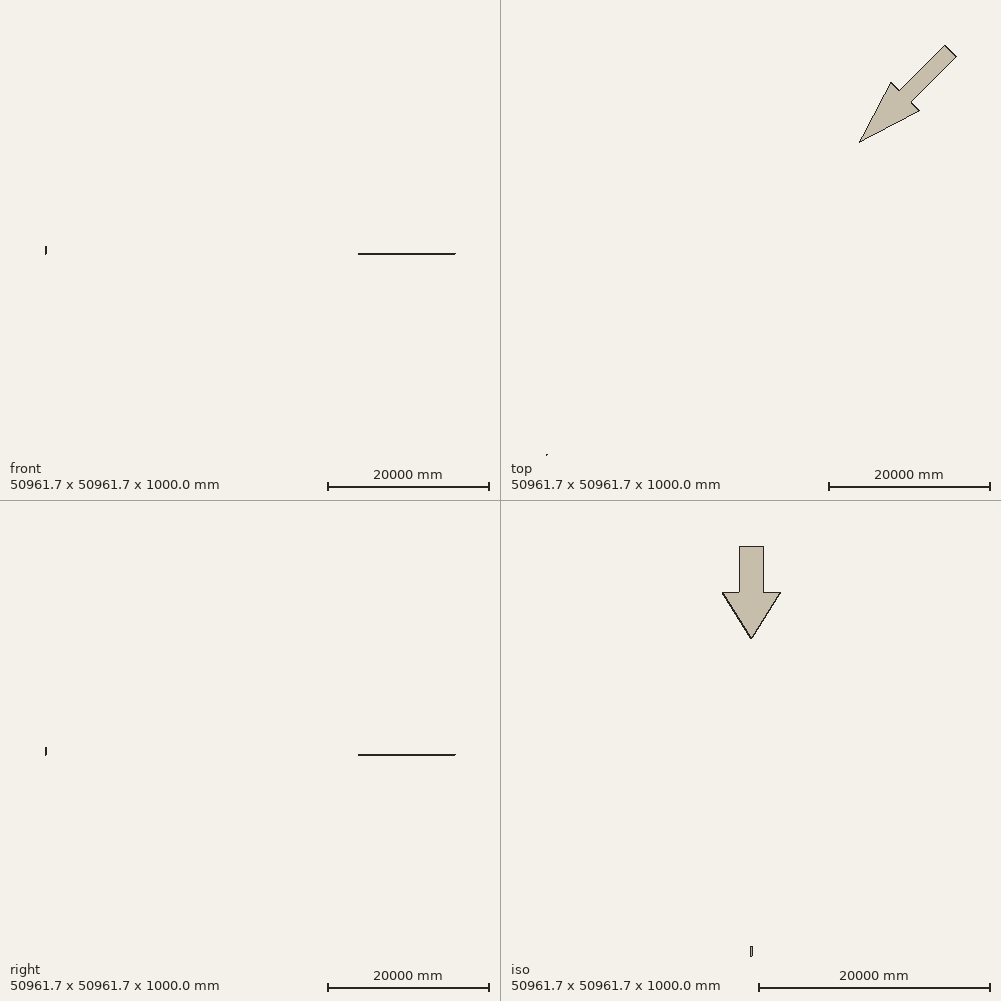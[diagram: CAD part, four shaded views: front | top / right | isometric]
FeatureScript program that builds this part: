
annotation { "Feature Type Name" : "Feature", "Feature Type Description" : "" }
export const myFeature = defineFeature(function(context is Context, id is Id, definition is map)
    precondition{}
    {
        {
            var Q0;
            Q0=qCreatedBy(makeId("Top.planeOp"),FACE);
            var sketch = newSketch(context, id + "F0", { "sketchPlane" : qUnion([Q0])});
            skLineSegment(sketch, "E0", {"start": v(0, -8.09) * mm, "end": v(0, 84.63) * mm, "construction": true});
            skLineSegment(sketch, "E1", {"start": v(-1000, 8000) * mm, "end": v(1000, 8000) * mm});
            skLineSegment(sketch, "E2", {"start": v(1000, 8000) * mm, "end": v(1000, 0) * mm});
            skLineSegment(sketch, "E3", {"start": v(1000, 0) * mm, "end": v(2500, 0) * mm});
            skLineSegment(sketch, "E4", {"start": v(2500, 0) * mm, "end": v(0, -8000) * mm});
            skLineSegment(sketch, "E5", {"start": v(0, -8000) * mm, "end": v(-2500, 0) * mm});
            skLineSegment(sketch, "E6", {"start": v(-2500, 0) * mm, "end": v(-1000, 0) * mm});
            skLineSegment(sketch, "E7", {"start": v(-1000, 0) * mm, "end": v(-1000, 8000) * mm});
            skSolve(sketch);
        }
        {
            var Q0;
            Q0 = qSketchRegion(id + "F0", true);
            extrude(context, id + "F1", {"entities" : qUnion([Q0]), "depth" : 100 * mm, "offsetDistance" : 25 * mm});
        }
        {
            var Q0;
            Q0=qCreatedBy(makeId("Top.planeOp"),FACE);
            var sketch = newSketch(context, id + "F2", { "sketchPlane" : qUnion([Q0])});
            skCircle(sketch, "E8", {"center": v(0, -63000) * mm, "radius": 50 * mm});
            skSolve(sketch);
        }
        {
            var Q0;
            Q0 = qSketchRegion(id + "F2", true);
            extrude(context, id + "F3", {"entities" : qUnion([Q0]), "depth" : 1000 * mm, "offsetDistance" : 25 * mm});
        }
        {
            var Q0;
            Q0=makeQuery(id+"F1.opExtrude","SWEPT_BODY",BODY,{"disambiguationData":[OSD([sQuery(id+"F0.wireOp",EDGE,"E1"),sQuery(id+"F0.wireOp",EDGE,"E2"),sQuery(id+"F0.wireOp",EDGE,"E3"),sQuery(id+"F0.wireOp",EDGE,"E4"),sQuery(id+"F0.wireOp",EDGE,"E5"),sQuery(id+"F0.wireOp",EDGE,"E6"),sQuery(id+"F0.wireOp",EDGE,"E7")])]});
            var Q1;
            Q1=makeQuery(id+"F1.opExtrude","SWEPT_BODY",BODY,{"disambiguationData":[OSD([sQuery(id+"F0.wireOp",EDGE,"40971db5-e6c9-45f8-a843-42a628b66c5b.sketch_text.stroke-86"),sQuery(id+"F0.wireOp",EDGE,"40971db5-e6c9-45f8-a843-42a628b66c5b.sketch_text.stroke-87"),sQuery(id+"F0.wireOp",EDGE,"40971db5-e6c9-45f8-a843-42a628b66c5b.sketch_text.stroke-88"),sQuery(id+"F0.wireOp",EDGE,"40971db5-e6c9-45f8-a843-42a628b66c5b.sketch_text.stroke-89")])]});
            var Q2;
            Q2=makeQuery(id+"F1.opExtrude","SWEPT_BODY",BODY,{"disambiguationData":[OSD([sQuery(id+"F0.wireOp",EDGE,"40971db5-e6c9-45f8-a843-42a628b66c5b.sketch_text.stroke-90"),sQuery(id+"F0.wireOp",EDGE,"40971db5-e6c9-45f8-a843-42a628b66c5b.sketch_text.stroke-91"),sQuery(id+"F0.wireOp",EDGE,"40971db5-e6c9-45f8-a843-42a628b66c5b.sketch_text.stroke-92"),sQuery(id+"F0.wireOp",EDGE,"40971db5-e6c9-45f8-a843-42a628b66c5b.sketch_text.stroke-93"),sQuery(id+"F0.wireOp",EDGE,"40971db5-e6c9-45f8-a843-42a628b66c5b.sketch_text.stroke-94"),sQuery(id+"F0.wireOp",EDGE,"40971db5-e6c9-45f8-a843-42a628b66c5b.sketch_text.stroke-95"),sQuery(id+"F0.wireOp",EDGE,"40971db5-e6c9-45f8-a843-42a628b66c5b.sketch_text.stroke-96"),sQuery(id+"F0.wireOp",EDGE,"40971db5-e6c9-45f8-a843-42a628b66c5b.sketch_text.stroke-97")])]});
            var Q3;
            Q3=makeQuery(id+"F1.opExtrude","SWEPT_BODY",BODY,{"disambiguationData":[OSD([sQuery(id+"F0.wireOp",EDGE,"40971db5-e6c9-45f8-a843-42a628b66c5b.sketch_text.stroke-32"),sQuery(id+"F0.wireOp",EDGE,"40971db5-e6c9-45f8-a843-42a628b66c5b.sketch_text.stroke-33"),sQuery(id+"F0.wireOp",EDGE,"40971db5-e6c9-45f8-a843-42a628b66c5b.sketch_text.stroke-34"),sQuery(id+"F0.wireOp",EDGE,"40971db5-e6c9-45f8-a843-42a628b66c5b.sketch_text.stroke-35"),sQuery(id+"F0.wireOp",EDGE,"40971db5-e6c9-45f8-a843-42a628b66c5b.sketch_text.stroke-36"),sQuery(id+"F0.wireOp",EDGE,"40971db5-e6c9-45f8-a843-42a628b66c5b.sketch_text.stroke-37"),sQuery(id+"F0.wireOp",EDGE,"40971db5-e6c9-45f8-a843-42a628b66c5b.sketch_text.stroke-38"),sQuery(id+"F0.wireOp",EDGE,"40971db5-e6c9-45f8-a843-42a628b66c5b.sketch_text.stroke-39"),sQuery(id+"F0.wireOp",EDGE,"40971db5-e6c9-45f8-a843-42a628b66c5b.sketch_text.stroke-40"),sQuery(id+"F0.wireOp",EDGE,"40971db5-e6c9-45f8-a843-42a628b66c5b.sketch_text.stroke-41"),sQuery(id+"F0.wireOp",EDGE,"40971db5-e6c9-45f8-a843-42a628b66c5b.sketch_text.stroke-42"),sQuery(id+"F0.wireOp",EDGE,"40971db5-e6c9-45f8-a843-42a628b66c5b.sketch_text.stroke-43"),sQuery(id+"F0.wireOp",EDGE,"40971db5-e6c9-45f8-a843-42a628b66c5b.sketch_text.stroke-44"),sQuery(id+"F0.wireOp",EDGE,"40971db5-e6c9-45f8-a843-42a628b66c5b.sketch_text.stroke-45"),sQuery(id+"F0.wireOp",EDGE,"40971db5-e6c9-45f8-a843-42a628b66c5b.sketch_text.stroke-46"),sQuery(id+"F0.wireOp",EDGE,"40971db5-e6c9-45f8-a843-42a628b66c5b.sketch_text.stroke-47"),sQuery(id+"F0.wireOp",EDGE,"40971db5-e6c9-45f8-a843-42a628b66c5b.sketch_text.stroke-48")])]});
            var Q4;
            Q4=makeQuery(id+"F1.opExtrude","SWEPT_BODY",BODY,{"disambiguationData":[OSD([sQuery(id+"F0.wireOp",EDGE,"40971db5-e6c9-45f8-a843-42a628b66c5b.sketch_text.stroke-73"),sQuery(id+"F0.wireOp",EDGE,"40971db5-e6c9-45f8-a843-42a628b66c5b.sketch_text.stroke-74"),sQuery(id+"F0.wireOp",EDGE,"40971db5-e6c9-45f8-a843-42a628b66c5b.sketch_text.stroke-75"),sQuery(id+"F0.wireOp",EDGE,"40971db5-e6c9-45f8-a843-42a628b66c5b.sketch_text.stroke-76"),sQuery(id+"F0.wireOp",EDGE,"40971db5-e6c9-45f8-a843-42a628b66c5b.sketch_text.stroke-77"),sQuery(id+"F0.wireOp",EDGE,"40971db5-e6c9-45f8-a843-42a628b66c5b.sketch_text.stroke-78"),sQuery(id+"F0.wireOp",EDGE,"40971db5-e6c9-45f8-a843-42a628b66c5b.sketch_text.stroke-79"),sQuery(id+"F0.wireOp",EDGE,"40971db5-e6c9-45f8-a843-42a628b66c5b.sketch_text.stroke-80"),sQuery(id+"F0.wireOp",EDGE,"40971db5-e6c9-45f8-a843-42a628b66c5b.sketch_text.stroke-81"),sQuery(id+"F0.wireOp",EDGE,"40971db5-e6c9-45f8-a843-42a628b66c5b.sketch_text.stroke-82"),sQuery(id+"F0.wireOp",EDGE,"40971db5-e6c9-45f8-a843-42a628b66c5b.sketch_text.stroke-83"),sQuery(id+"F0.wireOp",EDGE,"40971db5-e6c9-45f8-a843-42a628b66c5b.sketch_text.stroke-84"),sQuery(id+"F0.wireOp",EDGE,"40971db5-e6c9-45f8-a843-42a628b66c5b.sketch_text.stroke-85")])]});
            var Q5;
            Q5=makeQuery(id+"F1.opExtrude","SWEPT_BODY",BODY,{"disambiguationData":[OSD([sQuery(id+"F0.wireOp",EDGE,"40971db5-e6c9-45f8-a843-42a628b66c5b.sketch_text.stroke-113"),sQuery(id+"F0.wireOp",EDGE,"40971db5-e6c9-45f8-a843-42a628b66c5b.sketch_text.stroke-114"),sQuery(id+"F0.wireOp",EDGE,"40971db5-e6c9-45f8-a843-42a628b66c5b.sketch_text.stroke-115"),sQuery(id+"F0.wireOp",EDGE,"40971db5-e6c9-45f8-a843-42a628b66c5b.sketch_text.stroke-116"),sQuery(id+"F0.wireOp",EDGE,"40971db5-e6c9-45f8-a843-42a628b66c5b.sketch_text.stroke-117"),sQuery(id+"F0.wireOp",EDGE,"40971db5-e6c9-45f8-a843-42a628b66c5b.sketch_text.stroke-118"),sQuery(id+"F0.wireOp",EDGE,"40971db5-e6c9-45f8-a843-42a628b66c5b.sketch_text.stroke-119"),sQuery(id+"F0.wireOp",EDGE,"40971db5-e6c9-45f8-a843-42a628b66c5b.sketch_text.stroke-120"),sQuery(id+"F0.wireOp",EDGE,"40971db5-e6c9-45f8-a843-42a628b66c5b.sketch_text.stroke-121"),sQuery(id+"F0.wireOp",EDGE,"40971db5-e6c9-45f8-a843-42a628b66c5b.sketch_text.stroke-122"),sQuery(id+"F0.wireOp",EDGE,"40971db5-e6c9-45f8-a843-42a628b66c5b.sketch_text.stroke-123"),sQuery(id+"F0.wireOp",EDGE,"40971db5-e6c9-45f8-a843-42a628b66c5b.sketch_text.stroke-124"),sQuery(id+"F0.wireOp",EDGE,"40971db5-e6c9-45f8-a843-42a628b66c5b.sketch_text.stroke-125"),sQuery(id+"F0.wireOp",EDGE,"40971db5-e6c9-45f8-a843-42a628b66c5b.sketch_text.stroke-126"),sQuery(id+"F0.wireOp",EDGE,"40971db5-e6c9-45f8-a843-42a628b66c5b.sketch_text.stroke-127"),sQuery(id+"F0.wireOp",EDGE,"40971db5-e6c9-45f8-a843-42a628b66c5b.sketch_text.stroke-128"),sQuery(id+"F0.wireOp",EDGE,"40971db5-e6c9-45f8-a843-42a628b66c5b.sketch_text.stroke-129"),sQuery(id+"F0.wireOp",EDGE,"40971db5-e6c9-45f8-a843-42a628b66c5b.sketch_text.stroke-130")])]});
            var Q6;
            Q6=makeQuery(id+"F1.opExtrude","SWEPT_BODY",BODY,{"disambiguationData":[OSD([sQuery(id+"F0.wireOp",EDGE,"40971db5-e6c9-45f8-a843-42a628b66c5b.sketch_text.stroke-20"),sQuery(id+"F0.wireOp",EDGE,"40971db5-e6c9-45f8-a843-42a628b66c5b.sketch_text.stroke-21"),sQuery(id+"F0.wireOp",EDGE,"40971db5-e6c9-45f8-a843-42a628b66c5b.sketch_text.stroke-22"),sQuery(id+"F0.wireOp",EDGE,"40971db5-e6c9-45f8-a843-42a628b66c5b.sketch_text.stroke-23")])]});
            var Q7;
            Q7=makeQuery(id+"F1.opExtrude","SWEPT_BODY",BODY,{"disambiguationData":[OSD([sQuery(id+"F0.wireOp",EDGE,"40971db5-e6c9-45f8-a843-42a628b66c5b.sketch_text.stroke-98"),sQuery(id+"F0.wireOp",EDGE,"40971db5-e6c9-45f8-a843-42a628b66c5b.sketch_text.stroke-99"),sQuery(id+"F0.wireOp",EDGE,"40971db5-e6c9-45f8-a843-42a628b66c5b.sketch_text.stroke-100"),sQuery(id+"F0.wireOp",EDGE,"40971db5-e6c9-45f8-a843-42a628b66c5b.sketch_text.stroke-101"),sQuery(id+"F0.wireOp",EDGE,"40971db5-e6c9-45f8-a843-42a628b66c5b.sketch_text.stroke-102"),sQuery(id+"F0.wireOp",EDGE,"40971db5-e6c9-45f8-a843-42a628b66c5b.sketch_text.stroke-103"),sQuery(id+"F0.wireOp",EDGE,"40971db5-e6c9-45f8-a843-42a628b66c5b.sketch_text.stroke-104"),sQuery(id+"F0.wireOp",EDGE,"40971db5-e6c9-45f8-a843-42a628b66c5b.sketch_text.stroke-105"),sQuery(id+"F0.wireOp",EDGE,"40971db5-e6c9-45f8-a843-42a628b66c5b.sketch_text.stroke-106"),sQuery(id+"F0.wireOp",EDGE,"40971db5-e6c9-45f8-a843-42a628b66c5b.sketch_text.stroke-107"),sQuery(id+"F0.wireOp",EDGE,"40971db5-e6c9-45f8-a843-42a628b66c5b.sketch_text.stroke-108"),sQuery(id+"F0.wireOp",EDGE,"40971db5-e6c9-45f8-a843-42a628b66c5b.sketch_text.stroke-109"),sQuery(id+"F0.wireOp",EDGE,"40971db5-e6c9-45f8-a843-42a628b66c5b.sketch_text.stroke-110"),sQuery(id+"F0.wireOp",EDGE,"40971db5-e6c9-45f8-a843-42a628b66c5b.sketch_text.stroke-111"),sQuery(id+"F0.wireOp",EDGE,"40971db5-e6c9-45f8-a843-42a628b66c5b.sketch_text.stroke-112")])]});
            var Q8;
            Q8=makeQuery(id+"F1.opExtrude","SWEPT_BODY",BODY,{"disambiguationData":[OSD([sQuery(id+"F0.wireOp",EDGE,"40971db5-e6c9-45f8-a843-42a628b66c5b.sketch_text.stroke-184"),sQuery(id+"F0.wireOp",EDGE,"40971db5-e6c9-45f8-a843-42a628b66c5b.sketch_text.stroke-185"),sQuery(id+"F0.wireOp",EDGE,"40971db5-e6c9-45f8-a843-42a628b66c5b.sketch_text.stroke-186"),sQuery(id+"F0.wireOp",EDGE,"40971db5-e6c9-45f8-a843-42a628b66c5b.sketch_text.stroke-187"),sQuery(id+"F0.wireOp",EDGE,"40971db5-e6c9-45f8-a843-42a628b66c5b.sketch_text.stroke-188"),sQuery(id+"F0.wireOp",EDGE,"40971db5-e6c9-45f8-a843-42a628b66c5b.sketch_text.stroke-189"),sQuery(id+"F0.wireOp",EDGE,"40971db5-e6c9-45f8-a843-42a628b66c5b.sketch_text.stroke-190"),sQuery(id+"F0.wireOp",EDGE,"40971db5-e6c9-45f8-a843-42a628b66c5b.sketch_text.stroke-191"),sQuery(id+"F0.wireOp",EDGE,"40971db5-e6c9-45f8-a843-42a628b66c5b.sketch_text.stroke-192"),sQuery(id+"F0.wireOp",EDGE,"40971db5-e6c9-45f8-a843-42a628b66c5b.sketch_text.stroke-193"),sQuery(id+"F0.wireOp",EDGE,"40971db5-e6c9-45f8-a843-42a628b66c5b.sketch_text.stroke-194"),sQuery(id+"F0.wireOp",EDGE,"40971db5-e6c9-45f8-a843-42a628b66c5b.sketch_text.stroke-195"),sQuery(id+"F0.wireOp",EDGE,"40971db5-e6c9-45f8-a843-42a628b66c5b.sketch_text.stroke-196"),sQuery(id+"F0.wireOp",EDGE,"40971db5-e6c9-45f8-a843-42a628b66c5b.sketch_text.stroke-197"),sQuery(id+"F0.wireOp",EDGE,"40971db5-e6c9-45f8-a843-42a628b66c5b.sketch_text.stroke-198"),sQuery(id+"F0.wireOp",EDGE,"40971db5-e6c9-45f8-a843-42a628b66c5b.sketch_text.stroke-199"),sQuery(id+"F0.wireOp",EDGE,"40971db5-e6c9-45f8-a843-42a628b66c5b.sketch_text.stroke-200"),sQuery(id+"F0.wireOp",EDGE,"40971db5-e6c9-45f8-a843-42a628b66c5b.sketch_text.stroke-201"),sQuery(id+"F0.wireOp",EDGE,"40971db5-e6c9-45f8-a843-42a628b66c5b.sketch_text.stroke-202"),sQuery(id+"F0.wireOp",EDGE,"40971db5-e6c9-45f8-a843-42a628b66c5b.sketch_text.stroke-203"),sQuery(id+"F0.wireOp",EDGE,"40971db5-e6c9-45f8-a843-42a628b66c5b.sketch_text.stroke-204"),sQuery(id+"F0.wireOp",EDGE,"40971db5-e6c9-45f8-a843-42a628b66c5b.sketch_text.stroke-205"),sQuery(id+"F0.wireOp",EDGE,"40971db5-e6c9-45f8-a843-42a628b66c5b.sketch_text.stroke-206"),sQuery(id+"F0.wireOp",EDGE,"40971db5-e6c9-45f8-a843-42a628b66c5b.sketch_text.stroke-207"),sQuery(id+"F0.wireOp",EDGE,"40971db5-e6c9-45f8-a843-42a628b66c5b.sketch_text.stroke-208"),sQuery(id+"F0.wireOp",EDGE,"40971db5-e6c9-45f8-a843-42a628b66c5b.sketch_text.stroke-209"),sQuery(id+"F0.wireOp",EDGE,"40971db5-e6c9-45f8-a843-42a628b66c5b.sketch_text.stroke-210"),sQuery(id+"F0.wireOp",EDGE,"40971db5-e6c9-45f8-a843-42a628b66c5b.sketch_text.stroke-211"),sQuery(id+"F0.wireOp",EDGE,"40971db5-e6c9-45f8-a843-42a628b66c5b.sketch_text.stroke-212"),sQuery(id+"F0.wireOp",EDGE,"40971db5-e6c9-45f8-a843-42a628b66c5b.sketch_text.stroke-213"),sQuery(id+"F0.wireOp",EDGE,"40971db5-e6c9-45f8-a843-42a628b66c5b.sketch_text.stroke-214"),sQuery(id+"F0.wireOp",EDGE,"40971db5-e6c9-45f8-a843-42a628b66c5b.sketch_text.stroke-215"),sQuery(id+"F0.wireOp",EDGE,"40971db5-e6c9-45f8-a843-42a628b66c5b.sketch_text.stroke-216"),sQuery(id+"F0.wireOp",EDGE,"40971db5-e6c9-45f8-a843-42a628b66c5b.sketch_text.stroke-217"),sQuery(id+"F0.wireOp",EDGE,"40971db5-e6c9-45f8-a843-42a628b66c5b.sketch_text.stroke-218"),sQuery(id+"F0.wireOp",EDGE,"40971db5-e6c9-45f8-a843-42a628b66c5b.sketch_text.stroke-219"),sQuery(id+"F0.wireOp",EDGE,"40971db5-e6c9-45f8-a843-42a628b66c5b.sketch_text.stroke-220"),sQuery(id+"F0.wireOp",EDGE,"40971db5-e6c9-45f8-a843-42a628b66c5b.sketch_text.stroke-221"),sQuery(id+"F0.wireOp",EDGE,"40971db5-e6c9-45f8-a843-42a628b66c5b.sketch_text.stroke-222"),sQuery(id+"F0.wireOp",EDGE,"40971db5-e6c9-45f8-a843-42a628b66c5b.sketch_text.stroke-223"),sQuery(id+"F0.wireOp",EDGE,"40971db5-e6c9-45f8-a843-42a628b66c5b.sketch_text.stroke-224"),sQuery(id+"F0.wireOp",EDGE,"40971db5-e6c9-45f8-a843-42a628b66c5b.sketch_text.stroke-225"),sQuery(id+"F0.wireOp",EDGE,"40971db5-e6c9-45f8-a843-42a628b66c5b.sketch_text.stroke-226"),sQuery(id+"F0.wireOp",EDGE,"40971db5-e6c9-45f8-a843-42a628b66c5b.sketch_text.stroke-227")])]});
            var Q9;
            Q9=makeQuery(id+"F1.opExtrude","SWEPT_BODY",BODY,{"disambiguationData":[OSD([sQuery(id+"F0.wireOp",EDGE,"40971db5-e6c9-45f8-a843-42a628b66c5b.sketch_text.stroke-167"),sQuery(id+"F0.wireOp",EDGE,"40971db5-e6c9-45f8-a843-42a628b66c5b.sketch_text.stroke-168"),sQuery(id+"F0.wireOp",EDGE,"40971db5-e6c9-45f8-a843-42a628b66c5b.sketch_text.stroke-169"),sQuery(id+"F0.wireOp",EDGE,"40971db5-e6c9-45f8-a843-42a628b66c5b.sketch_text.stroke-170"),sQuery(id+"F0.wireOp",EDGE,"40971db5-e6c9-45f8-a843-42a628b66c5b.sketch_text.stroke-171"),sQuery(id+"F0.wireOp",EDGE,"40971db5-e6c9-45f8-a843-42a628b66c5b.sketch_text.stroke-172"),sQuery(id+"F0.wireOp",EDGE,"40971db5-e6c9-45f8-a843-42a628b66c5b.sketch_text.stroke-173"),sQuery(id+"F0.wireOp",EDGE,"40971db5-e6c9-45f8-a843-42a628b66c5b.sketch_text.stroke-174"),sQuery(id+"F0.wireOp",EDGE,"40971db5-e6c9-45f8-a843-42a628b66c5b.sketch_text.stroke-175"),sQuery(id+"F0.wireOp",EDGE,"40971db5-e6c9-45f8-a843-42a628b66c5b.sketch_text.stroke-176"),sQuery(id+"F0.wireOp",EDGE,"40971db5-e6c9-45f8-a843-42a628b66c5b.sketch_text.stroke-177"),sQuery(id+"F0.wireOp",EDGE,"40971db5-e6c9-45f8-a843-42a628b66c5b.sketch_text.stroke-178"),sQuery(id+"F0.wireOp",EDGE,"40971db5-e6c9-45f8-a843-42a628b66c5b.sketch_text.stroke-179"),sQuery(id+"F0.wireOp",EDGE,"40971db5-e6c9-45f8-a843-42a628b66c5b.sketch_text.stroke-180"),sQuery(id+"F0.wireOp",EDGE,"40971db5-e6c9-45f8-a843-42a628b66c5b.sketch_text.stroke-181"),sQuery(id+"F0.wireOp",EDGE,"40971db5-e6c9-45f8-a843-42a628b66c5b.sketch_text.stroke-182"),sQuery(id+"F0.wireOp",EDGE,"40971db5-e6c9-45f8-a843-42a628b66c5b.sketch_text.stroke-183")])]});
            var Q10;
            Q10=makeQuery(id+"F1.opExtrude","SWEPT_BODY",BODY,{"disambiguationData":[OSD([sQuery(id+"F0.wireOp",EDGE,"40971db5-e6c9-45f8-a843-42a628b66c5b.sketch_text.stroke-150"),sQuery(id+"F0.wireOp",EDGE,"40971db5-e6c9-45f8-a843-42a628b66c5b.sketch_text.stroke-151"),sQuery(id+"F0.wireOp",EDGE,"40971db5-e6c9-45f8-a843-42a628b66c5b.sketch_text.stroke-152"),sQuery(id+"F0.wireOp",EDGE,"40971db5-e6c9-45f8-a843-42a628b66c5b.sketch_text.stroke-153"),sQuery(id+"F0.wireOp",EDGE,"40971db5-e6c9-45f8-a843-42a628b66c5b.sketch_text.stroke-154"),sQuery(id+"F0.wireOp",EDGE,"40971db5-e6c9-45f8-a843-42a628b66c5b.sketch_text.stroke-155"),sQuery(id+"F0.wireOp",EDGE,"40971db5-e6c9-45f8-a843-42a628b66c5b.sketch_text.stroke-156"),sQuery(id+"F0.wireOp",EDGE,"40971db5-e6c9-45f8-a843-42a628b66c5b.sketch_text.stroke-157"),sQuery(id+"F0.wireOp",EDGE,"40971db5-e6c9-45f8-a843-42a628b66c5b.sketch_text.stroke-158"),sQuery(id+"F0.wireOp",EDGE,"40971db5-e6c9-45f8-a843-42a628b66c5b.sketch_text.stroke-159"),sQuery(id+"F0.wireOp",EDGE,"40971db5-e6c9-45f8-a843-42a628b66c5b.sketch_text.stroke-160"),sQuery(id+"F0.wireOp",EDGE,"40971db5-e6c9-45f8-a843-42a628b66c5b.sketch_text.stroke-161"),sQuery(id+"F0.wireOp",EDGE,"40971db5-e6c9-45f8-a843-42a628b66c5b.sketch_text.stroke-162"),sQuery(id+"F0.wireOp",EDGE,"40971db5-e6c9-45f8-a843-42a628b66c5b.sketch_text.stroke-163"),sQuery(id+"F0.wireOp",EDGE,"40971db5-e6c9-45f8-a843-42a628b66c5b.sketch_text.stroke-164"),sQuery(id+"F0.wireOp",EDGE,"40971db5-e6c9-45f8-a843-42a628b66c5b.sketch_text.stroke-165"),sQuery(id+"F0.wireOp",EDGE,"40971db5-e6c9-45f8-a843-42a628b66c5b.sketch_text.stroke-166")])]});
            var Q11;
            Q11=makeQuery(id+"F1.opExtrude","SWEPT_BODY",BODY,{"disambiguationData":[OSD([sQuery(id+"F0.wireOp",EDGE,"40971db5-e6c9-45f8-a843-42a628b66c5b.sketch_text.stroke-24"),sQuery(id+"F0.wireOp",EDGE,"40971db5-e6c9-45f8-a843-42a628b66c5b.sketch_text.stroke-25"),sQuery(id+"F0.wireOp",EDGE,"40971db5-e6c9-45f8-a843-42a628b66c5b.sketch_text.stroke-26"),sQuery(id+"F0.wireOp",EDGE,"40971db5-e6c9-45f8-a843-42a628b66c5b.sketch_text.stroke-27"),sQuery(id+"F0.wireOp",EDGE,"40971db5-e6c9-45f8-a843-42a628b66c5b.sketch_text.stroke-28"),sQuery(id+"F0.wireOp",EDGE,"40971db5-e6c9-45f8-a843-42a628b66c5b.sketch_text.stroke-29"),sQuery(id+"F0.wireOp",EDGE,"40971db5-e6c9-45f8-a843-42a628b66c5b.sketch_text.stroke-30"),sQuery(id+"F0.wireOp",EDGE,"40971db5-e6c9-45f8-a843-42a628b66c5b.sketch_text.stroke-31")])]});
            var Q12;
            Q12=makeQuery(id+"F1.opExtrude","SWEPT_BODY",BODY,{"disambiguationData":[OSD([sQuery(id+"F0.wireOp",EDGE,"40971db5-e6c9-45f8-a843-42a628b66c5b.sketch_text.stroke-0"),sQuery(id+"F0.wireOp",EDGE,"40971db5-e6c9-45f8-a843-42a628b66c5b.sketch_text.stroke-1"),sQuery(id+"F0.wireOp",EDGE,"40971db5-e6c9-45f8-a843-42a628b66c5b.sketch_text.stroke-2"),sQuery(id+"F0.wireOp",EDGE,"40971db5-e6c9-45f8-a843-42a628b66c5b.sketch_text.stroke-3"),sQuery(id+"F0.wireOp",EDGE,"40971db5-e6c9-45f8-a843-42a628b66c5b.sketch_text.stroke-4"),sQuery(id+"F0.wireOp",EDGE,"40971db5-e6c9-45f8-a843-42a628b66c5b.sketch_text.stroke-5"),sQuery(id+"F0.wireOp",EDGE,"40971db5-e6c9-45f8-a843-42a628b66c5b.sketch_text.stroke-6"),sQuery(id+"F0.wireOp",EDGE,"40971db5-e6c9-45f8-a843-42a628b66c5b.sketch_text.stroke-7"),sQuery(id+"F0.wireOp",EDGE,"40971db5-e6c9-45f8-a843-42a628b66c5b.sketch_text.stroke-8"),sQuery(id+"F0.wireOp",EDGE,"40971db5-e6c9-45f8-a843-42a628b66c5b.sketch_text.stroke-9"),sQuery(id+"F0.wireOp",EDGE,"40971db5-e6c9-45f8-a843-42a628b66c5b.sketch_text.stroke-10"),sQuery(id+"F0.wireOp",EDGE,"40971db5-e6c9-45f8-a843-42a628b66c5b.sketch_text.stroke-11"),sQuery(id+"F0.wireOp",EDGE,"40971db5-e6c9-45f8-a843-42a628b66c5b.sketch_text.stroke-12"),sQuery(id+"F0.wireOp",EDGE,"40971db5-e6c9-45f8-a843-42a628b66c5b.sketch_text.stroke-13"),sQuery(id+"F0.wireOp",EDGE,"40971db5-e6c9-45f8-a843-42a628b66c5b.sketch_text.stroke-14"),sQuery(id+"F0.wireOp",EDGE,"40971db5-e6c9-45f8-a843-42a628b66c5b.sketch_text.stroke-15"),sQuery(id+"F0.wireOp",EDGE,"40971db5-e6c9-45f8-a843-42a628b66c5b.sketch_text.stroke-16"),sQuery(id+"F0.wireOp",EDGE,"40971db5-e6c9-45f8-a843-42a628b66c5b.sketch_text.stroke-17"),sQuery(id+"F0.wireOp",EDGE,"40971db5-e6c9-45f8-a843-42a628b66c5b.sketch_text.stroke-18"),sQuery(id+"F0.wireOp",EDGE,"40971db5-e6c9-45f8-a843-42a628b66c5b.sketch_text.stroke-19")])]});
            var Q13;
            Q13=makeQuery(id+"F1.opExtrude","SWEPT_BODY",BODY,{"disambiguationData":[OSD([sQuery(id+"F0.wireOp",EDGE,"40971db5-e6c9-45f8-a843-42a628b66c5b.sketch_text.stroke-131"),sQuery(id+"F0.wireOp",EDGE,"40971db5-e6c9-45f8-a843-42a628b66c5b.sketch_text.stroke-132"),sQuery(id+"F0.wireOp",EDGE,"40971db5-e6c9-45f8-a843-42a628b66c5b.sketch_text.stroke-133"),sQuery(id+"F0.wireOp",EDGE,"40971db5-e6c9-45f8-a843-42a628b66c5b.sketch_text.stroke-134"),sQuery(id+"F0.wireOp",EDGE,"40971db5-e6c9-45f8-a843-42a628b66c5b.sketch_text.stroke-135"),sQuery(id+"F0.wireOp",EDGE,"40971db5-e6c9-45f8-a843-42a628b66c5b.sketch_text.stroke-136"),sQuery(id+"F0.wireOp",EDGE,"40971db5-e6c9-45f8-a843-42a628b66c5b.sketch_text.stroke-137"),sQuery(id+"F0.wireOp",EDGE,"40971db5-e6c9-45f8-a843-42a628b66c5b.sketch_text.stroke-138"),sQuery(id+"F0.wireOp",EDGE,"40971db5-e6c9-45f8-a843-42a628b66c5b.sketch_text.stroke-139"),sQuery(id+"F0.wireOp",EDGE,"40971db5-e6c9-45f8-a843-42a628b66c5b.sketch_text.stroke-140"),sQuery(id+"F0.wireOp",EDGE,"40971db5-e6c9-45f8-a843-42a628b66c5b.sketch_text.stroke-141"),sQuery(id+"F0.wireOp",EDGE,"40971db5-e6c9-45f8-a843-42a628b66c5b.sketch_text.stroke-142"),sQuery(id+"F0.wireOp",EDGE,"40971db5-e6c9-45f8-a843-42a628b66c5b.sketch_text.stroke-143"),sQuery(id+"F0.wireOp",EDGE,"40971db5-e6c9-45f8-a843-42a628b66c5b.sketch_text.stroke-144"),sQuery(id+"F0.wireOp",EDGE,"40971db5-e6c9-45f8-a843-42a628b66c5b.sketch_text.stroke-145"),sQuery(id+"F0.wireOp",EDGE,"40971db5-e6c9-45f8-a843-42a628b66c5b.sketch_text.stroke-146"),sQuery(id+"F0.wireOp",EDGE,"40971db5-e6c9-45f8-a843-42a628b66c5b.sketch_text.stroke-147"),sQuery(id+"F0.wireOp",EDGE,"40971db5-e6c9-45f8-a843-42a628b66c5b.sketch_text.stroke-148"),sQuery(id+"F0.wireOp",EDGE,"40971db5-e6c9-45f8-a843-42a628b66c5b.sketch_text.stroke-149")])]});
            var Q14;
            Q14=makeQuery(id+"F1.opExtrude","SWEPT_BODY",BODY,{"disambiguationData":[OSD([sQuery(id+"F0.wireOp",EDGE,"40971db5-e6c9-45f8-a843-42a628b66c5b.sketch_text.stroke-49"),sQuery(id+"F0.wireOp",EDGE,"40971db5-e6c9-45f8-a843-42a628b66c5b.sketch_text.stroke-50"),sQuery(id+"F0.wireOp",EDGE,"40971db5-e6c9-45f8-a843-42a628b66c5b.sketch_text.stroke-51"),sQuery(id+"F0.wireOp",EDGE,"40971db5-e6c9-45f8-a843-42a628b66c5b.sketch_text.stroke-52"),sQuery(id+"F0.wireOp",EDGE,"40971db5-e6c9-45f8-a843-42a628b66c5b.sketch_text.stroke-53"),sQuery(id+"F0.wireOp",EDGE,"40971db5-e6c9-45f8-a843-42a628b66c5b.sketch_text.stroke-54"),sQuery(id+"F0.wireOp",EDGE,"40971db5-e6c9-45f8-a843-42a628b66c5b.sketch_text.stroke-55"),sQuery(id+"F0.wireOp",EDGE,"40971db5-e6c9-45f8-a843-42a628b66c5b.sketch_text.stroke-56"),sQuery(id+"F0.wireOp",EDGE,"40971db5-e6c9-45f8-a843-42a628b66c5b.sketch_text.stroke-57"),sQuery(id+"F0.wireOp",EDGE,"40971db5-e6c9-45f8-a843-42a628b66c5b.sketch_text.stroke-58"),sQuery(id+"F0.wireOp",EDGE,"40971db5-e6c9-45f8-a843-42a628b66c5b.sketch_text.stroke-59"),sQuery(id+"F0.wireOp",EDGE,"40971db5-e6c9-45f8-a843-42a628b66c5b.sketch_text.stroke-60"),sQuery(id+"F0.wireOp",EDGE,"40971db5-e6c9-45f8-a843-42a628b66c5b.sketch_text.stroke-61"),sQuery(id+"F0.wireOp",EDGE,"40971db5-e6c9-45f8-a843-42a628b66c5b.sketch_text.stroke-62"),sQuery(id+"F0.wireOp",EDGE,"40971db5-e6c9-45f8-a843-42a628b66c5b.sketch_text.stroke-63"),sQuery(id+"F0.wireOp",EDGE,"40971db5-e6c9-45f8-a843-42a628b66c5b.sketch_text.stroke-64"),sQuery(id+"F0.wireOp",EDGE,"40971db5-e6c9-45f8-a843-42a628b66c5b.sketch_text.stroke-65"),sQuery(id+"F0.wireOp",EDGE,"40971db5-e6c9-45f8-a843-42a628b66c5b.sketch_text.stroke-66"),sQuery(id+"F0.wireOp",EDGE,"40971db5-e6c9-45f8-a843-42a628b66c5b.sketch_text.stroke-67"),sQuery(id+"F0.wireOp",EDGE,"40971db5-e6c9-45f8-a843-42a628b66c5b.sketch_text.stroke-68"),sQuery(id+"F0.wireOp",EDGE,"40971db5-e6c9-45f8-a843-42a628b66c5b.sketch_text.stroke-69"),sQuery(id+"F0.wireOp",EDGE,"40971db5-e6c9-45f8-a843-42a628b66c5b.sketch_text.stroke-70"),sQuery(id+"F0.wireOp",EDGE,"40971db5-e6c9-45f8-a843-42a628b66c5b.sketch_text.stroke-71"),sQuery(id+"F0.wireOp",EDGE,"40971db5-e6c9-45f8-a843-42a628b66c5b.sketch_text.stroke-72")])]});
            var Q15;
            Q15=makeQuery(id+"F3.opExtrude","SWEPT_FACE",FACE,{"disambiguationData":[OSD([sQuery(id+"F2.wireOp",EDGE,"E8")])]});
            transform(context, id + "F4", {"entities" : qUnion([Q0, Q1, Q2, Q3, Q4, Q5, Q6, Q7, Q8, Q9, Q10, Q11, Q12, Q13, Q14]), "transformType" : TransformType.ROTATION, "transformAxis" : qUnion([Q15]), "angle" : 45 * degree, "makeCopy" : false});
        }
    });
